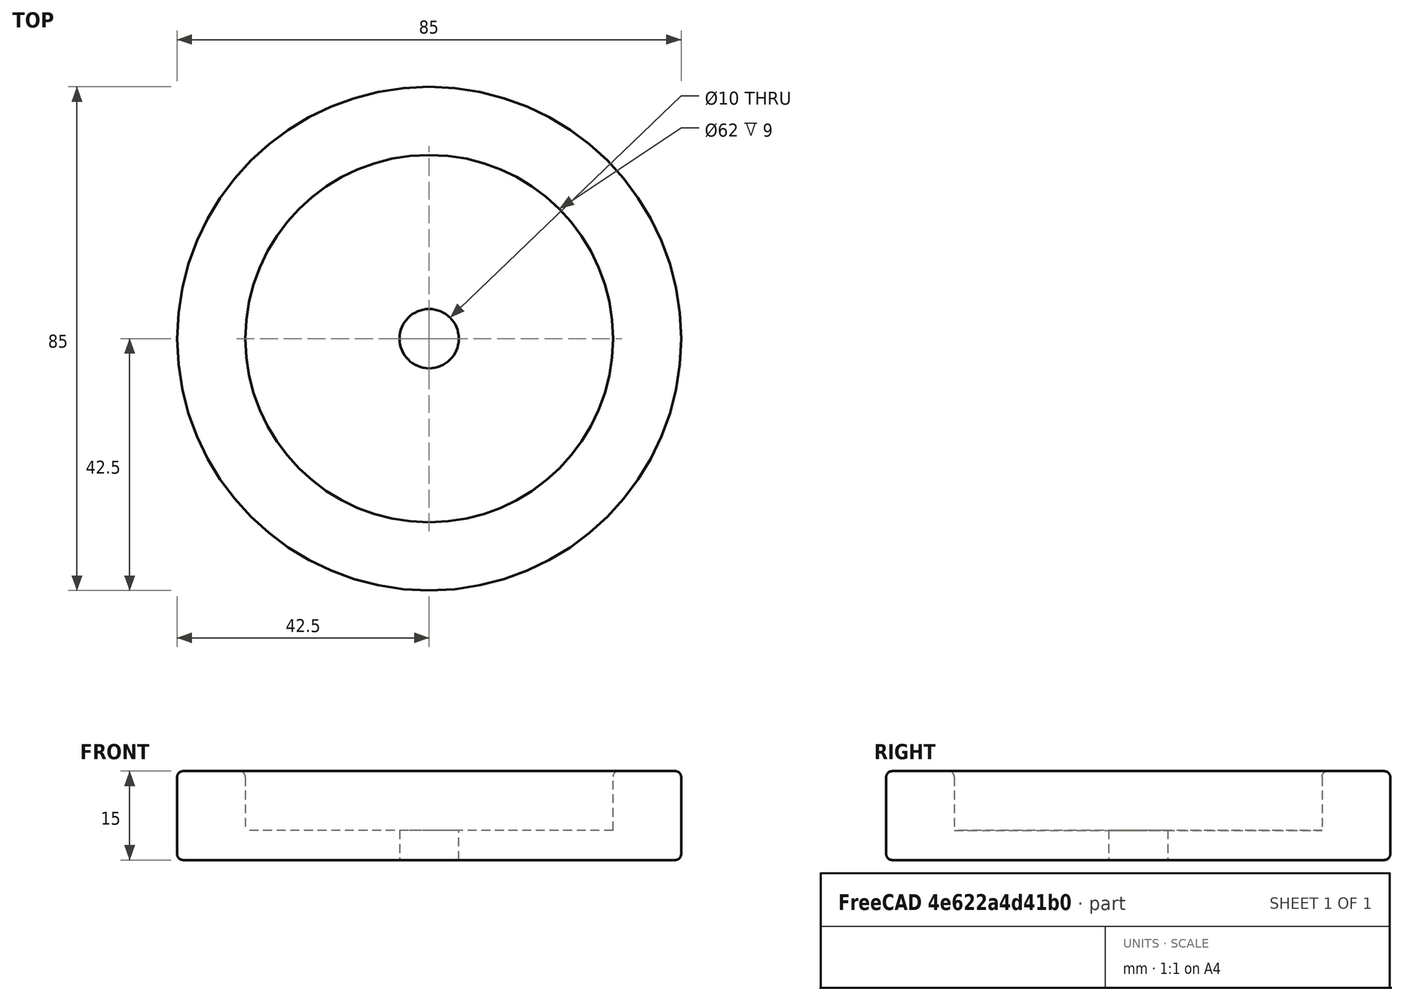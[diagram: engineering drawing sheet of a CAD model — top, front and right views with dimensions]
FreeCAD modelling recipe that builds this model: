
FCSTD DOCUMENT  (FreeCAD 1.0R39319 (Git))
Label: LGWasher
License: All rights reserved
LicenseURL: http://en.wikipedia.org/wiki/All_rights_reserved
objects: Sketcher::SketchObject×3, PartDesign::Pocket×2, Spreadsheet::Sheet×1, PartDesign::Pad×1, PartDesign::Fillet×1, PartDesign::Body×1, App::Part×1, Mesh::Feature×1
note: 19 computed .brp shape members not serialized (recipe doc carries the construction recipe); baked Part::Feature solids carry a one-line shape summary decoded from their .brp

FEATURE [Sketcher::SketchObject] Sketch  label="Sketch_Base"
  ArcFitTolerance = 1e-06
  AttachmentSupport = -> [XY_Plane001]
  FullyConstrained = true
  MakeInternals = false
  MapMode = 5
  expr: Constraints[1] = <<Spreadsheet>>.OD
  sketch-geometry (1):
    g0: Circle CenterX=0 CenterY=0 CenterZ=0 NormalX=0 NormalY=0 NormalZ=1 AngleXU=0 Radius=42.5
  constraints (2):
    c: Coincident(g0,g-1)
    c: Diameter(g0) = 85
FEATURE [Spreadsheet::Sheet] Spreadsheet
  cells = A1='HoleDia; B1(HoleDia)=10; A2='Thick; B2(Thick)=5; A3='ID; B3(ID)=62; A4='OD; B4(OD)=85; A5='Lip; B5(Lip)=10
FEATURE [PartDesign::Pad] Pad  label="Pad_Base"
  Direction = (0,0,1)
  Length = 15
  Length2 = 10
  Profile = -> Sketch
  ReferenceAxis = -> Sketch [N_Axis]
  Suppressed = false
  Type = 0
  expr: Length = <<Spreadsheet>>.Thick + <<Spreadsheet>>.Lip
FEATURE [Sketcher::SketchObject] Sketch001  label="Sketch_Hole"
  ArcFitTolerance = 1e-06
  AttachmentSupport = -> [XY_Plane001]
  FullyConstrained = true
  MakeInternals = false
  MapMode = 5
  expr: Constraints[1] = <<Spreadsheet>>.HoleDia
  sketch-geometry (1):
    g0: Circle CenterX=0 CenterY=0 CenterZ=0 NormalX=0 NormalY=0 NormalZ=1 AngleXU=0 Radius=5
  constraints (2):
    c: Coincident(g0,g-1)
    c: Diameter(g0) = 10
FEATURE [PartDesign::Pocket] Pocket  label="Pocket_Hole"
  BaseFeature = -> Pad
  Direction = (0,0,-1)
  Length = 10
  Length2 = 5
  Profile = -> Sketch001
  ReferenceAxis = -> Sketch001 [N_Axis]
  Reversed = true
  Suppressed = false
  Type = 1
  expr: Length = 10
FEATURE [Sketcher::SketchObject] Sketch002  label="Sketch_Removal"
  ArcFitTolerance = 1e-06
  AttachmentOffset = pos=(0,0,5) rot=(0,0,1;0rad)
  AttachmentSupport = -> [XY_Plane001]
  FullyConstrained = true
  MakeInternals = false
  MapMode = 5
  Placement = pos=(0,0,5) rot=(0,0,1;0rad)
  expr: .AttachmentOffset.Base.z = <<Spreadsheet>>.Thick
  expr: Constraints[1] = <<Spreadsheet>>.ID
  sketch-geometry (1):
    g0: Circle CenterX=0 CenterY=0 CenterZ=0 NormalX=0 NormalY=0 NormalZ=1 AngleXU=0 Radius=31
  constraints (2):
    c: Coincident(g0,g-1)
    c: Diameter(g0) = 62
FEATURE [PartDesign::Pocket] Pocket001  label="Pocket_Removal"
  BaseFeature = -> Pocket
  Direction = (0,0,-1)
  Length = 5
  Length2 = 5
  Profile = -> Sketch002
  ReferenceAxis = -> Sketch002 [N_Axis]
  Reversed = true
  Suppressed = false
  Type = 1
FEATURE [PartDesign::Fillet] Fillet
  Base = -> Pocket001 [Edge2,Edge3,Edge5]
  BaseFeature = -> Pocket001
  Radius = 1
  SupportTransform = false
  Suppressed = false
  UseAllEdges = false
FEATURE [PartDesign::Body] Body
  AllowCompound = false
  Group = -> [Sketch,Pad,Sketch001,Pocket,Sketch002,Pocket001,Fillet]
  Origin = -> Origin001
  Tip = -> Fillet
FEATURE [App::Part] Part
  Group = -> [Body]
  Origin = -> Origin
FEATURE [Mesh::Feature] Mesh  label="Fillet (Meshed)"
